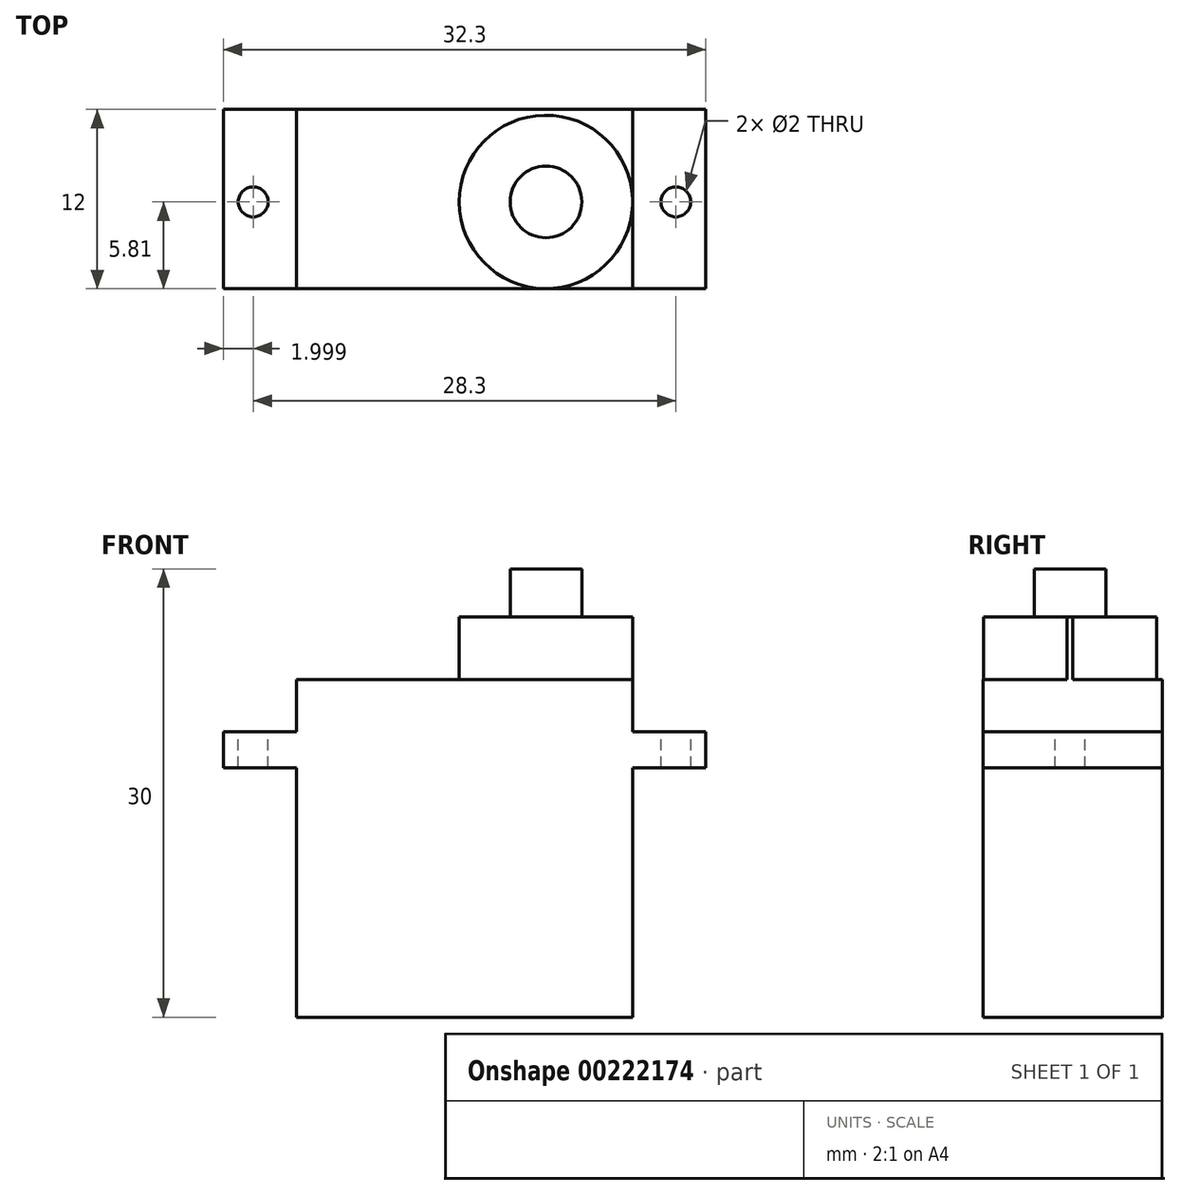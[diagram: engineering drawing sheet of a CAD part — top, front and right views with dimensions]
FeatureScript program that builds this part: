
annotation { "Feature Type Name" : "Feature", "Feature Type Description" : "" }
export const myFeature = defineFeature(function(context is Context, id is Id, definition is map)
    precondition{}
    {
        {
            var Q0;
            Q0=qCreatedBy(makeId("Top.planeOp"),FACE);
            var sketch = newSketch(context, id + "F0", { "sketchPlane" : qUnion([Q0])});
            skLineSegment(sketch, "E0.bottom", {"start": v(-11.12, 6.19) * mm, "end": v(21.18, 6.19) * mm});
            skLineSegment(sketch, "E0.top", {"start": v(-11.12, -5.81) * mm, "end": v(21.18, -5.81) * mm});
            skLineSegment(sketch, "E0.left", {"start": v(-11.12, 6.19) * mm, "end": v(-11.12, -5.81) * mm});
            skLineSegment(sketch, "E0.right", {"start": v(21.18, 6.19) * mm, "end": v(21.18, -5.81) * mm});
            skSolve(sketch);
        }
        {
            var Q0;
            Q0=makeQuery(id+"F0.imprint","IMPRINT",FACE,{"disambiguationData":[TD([[makeQuery(id+"F0.imprint","IMPRINT",EDGE,{"derivedFrom":sQuery(id+"F0.wireOp",EDGE,"E0.bottom")}),-1.0]])]});
            extrude(context, id + "F1", {"entities" : qUnion([Q0]), "depth" : 2.4 * mm});
        }
        {
            var Q0;
            Q0=makeQuery(id+"F1.opExtrude","CAP_FACE",FACE,{"disambiguationData":[OSD([sQuery(id+"F0.wireOp",EDGE,"E0.bottom"),sQuery(id+"F0.wireOp",EDGE,"E0.top"),sQuery(id+"F0.wireOp",EDGE,"E0.left"),sQuery(id+"F0.wireOp",EDGE,"E0.right")])],"isStart":false});
            var sketch = newSketch(context, id + "F2", { "sketchPlane" : qUnion([Q0])});
            skLineSegment(sketch, "E1.bottom", {"start": v(-6.22, 6.19) * mm, "end": v(16.28, 6.19) * mm});
            skLineSegment(sketch, "E1.top", {"start": v(-6.22, -5.81) * mm, "end": v(16.28, -5.81) * mm});
            skLineSegment(sketch, "E1.left", {"start": v(-6.22, 6.19) * mm, "end": v(-6.22, -5.81) * mm});
            skLineSegment(sketch, "E1.right", {"start": v(16.28, 6.19) * mm, "end": v(16.28, -5.81) * mm});
            skLineSegment(sketch, "E2", {"start": v(5.03, 6.19) * mm, "end": v(5.03, -10) * mm, "construction": true});
            skPoint(sketch, "E2.endSnap0", {"position": v(5.03, -5.81) * mm});
            skSolve(sketch);
        }
        {
            var Q0;
            Q0=makeQuery(id+"F2.imprint","IMPRINT",FACE,{"disambiguationData":[TD([[makeQuery(id+"F2.imprint","IMPRINT",EDGE,{"derivedFrom":sQuery(id+"F2.wireOp",EDGE,"E1.bottom")}),-1.0]])]});
            extrude(context, id + "F3", {"entities" : qUnion([Q0]), "operationType" : NewBodyOperationType.ADD, "depth" : 3.5 * mm});
        }
        {
            var Q0;
            Q0=makeQuery(id+"F3.opExtrude","CAP_FACE",FACE,{"disambiguationData":[OSD([sQuery(id+"F2.wireOp",EDGE,"E1.bottom"),sQuery(id+"F2.wireOp",EDGE,"E1.top"),sQuery(id+"F2.wireOp",EDGE,"E1.left"),sQuery(id+"F2.wireOp",EDGE,"E1.right")])],"isStart":false});
            extrude(context, id + "F4", {"entities" : qUnion([Q0]), "operationType" : NewBodyOperationType.ADD, "oppositeDirection" : true, "depth" : 22.6 * mm});
        }
        {
            var Q0;
            Q0=makeQuery(id+"F3.opExtrude","CAP_FACE",FACE,{"disambiguationData":[OSD([sQuery(id+"F2.wireOp",EDGE,"E1.bottom"),sQuery(id+"F2.wireOp",EDGE,"E1.top"),sQuery(id+"F2.wireOp",EDGE,"E1.left"),sQuery(id+"F2.wireOp",EDGE,"E1.right")])],"isStart":false});
            var sketch = newSketch(context, id + "F5", { "sketchPlane" : qUnion([Q0])});
            skCircle(sketch, "E3", {"center": v(10.48, 0) * mm, "radius": 5.8 * mm});
            skSolve(sketch);
        }
        {
            var Q0;
            {var subQ0=sQuery(id+"F5.wireOp",EDGE,"E3");var subQ1=makeQuery(id+"F3.opExtrude","CAP_EDGE",EDGE,{"disambiguationData":[OSD([sQuery(id+"F2.wireOp",EDGE,"E1.right")])],"isStart":false});var subQ2=makeQuery(id+"F5.imprint","INTERSECT",VERTEX,{"disambiguationData":[OD(0.0)],"derivedFrom":[subQ1,subQ0]});Q0=makeQuery(id+"F5.imprint","IMPRINT",FACE,{"disambiguationData":[TD([[makeQuery(id+"F5.imprint","IMPRINT",EDGE,{"disambiguationData":[TD([[subQ2,-1.0]])],"derivedFrom":subQ0}),1.0]])]});}
            extrude(context, id + "F6", {"entities" : qUnion([Q0]), "operationType" : NewBodyOperationType.ADD, "depth" : 4.2 * mm});
        }
        {
            var Q0;
            Q0=makeQuery(id+"F6.opExtrude","CAP_FACE",FACE,{"disambiguationData":[OSD([sQuery(id+"F2.wireOp",EDGE,"E1.right"),sQuery(id+"F5.wireOp",EDGE,"E3")])],"isStart":false});
            var sketch = newSketch(context, id + "F7", { "sketchPlane" : qUnion([Q0])});
            skCircle(sketch, "E4", {"center": v(10.48, 0) * mm, "radius": 2.4 * mm});
            skSolve(sketch);
        }
        {
            var Q0;
            Q0=makeQuery(id+"F7.imprint","IMPRINT",FACE,{"disambiguationData":[TD([[makeQuery(id+"F7.imprint","IMPRINT",EDGE,{"derivedFrom":sQuery(id+"F7.wireOp",EDGE,"E4")}),1.0]])]});
            extrude(context, id + "F8", {"entities" : qUnion([Q0]), "operationType" : NewBodyOperationType.ADD, "depth" : 3.2 * mm});
        }
        {
            var Q0;
            {var subQ0=sQuery(id+"F0.wireOp",EDGE,"E0.left");var subQ1=sQuery(id+"F0.wireOp",EDGE,"E0.top");var subQ2=sQuery(id+"F0.wireOp",EDGE,"E0.bottom");Q0=makeQuery(id+"F3.boolean.opBoolean","SPLIT",FACE,{"disambiguationData":[TD([makeQuery(id+"F1.opExtrude","SWEPT_FACE",FACE,{"disambiguationData":[OSD([subQ0])]})])],"derivedFrom":makeQuery(id+"F1.opExtrude","CAP_FACE",FACE,{"disambiguationData":[OSD([subQ2,subQ1,subQ0,sQuery(id+"F0.wireOp",EDGE,"E0.right")])],"isStart":false})});}
            var sketch = newSketch(context, id + "F9", { "sketchPlane" : qUnion([Q0])});
            skCircle(sketch, "E5", {"center": v(-9.12, 0) * mm, "radius": 1 * mm});
            skCircle(sketch, "E6", {"center": v(19.18, 0) * mm, "radius": 1 * mm});
            skSolve(sketch);
        }
        {
            var Q0;
            Q0=makeQuery(id+"F9.imprint","IMPRINT",FACE,{"disambiguationData":[TD([[makeQuery(id+"F9.imprint","IMPRINT",EDGE,{"derivedFrom":sQuery(id+"F9.wireOp",EDGE,"E5")}),1.0]])]});
            var Q1;
            Q1=makeQuery(id+"F9.imprint","IMPRINT",FACE,{"disambiguationData":[TD([[makeQuery(id+"F9.imprint","IMPRINT",EDGE,{"derivedFrom":sQuery(id+"F9.wireOp",EDGE,"E6")}),1.0]])]});
            extrude(context, id + "F10", {"entities" : qUnion([Q0, Q1]), "operationType" : NewBodyOperationType.REMOVE, "oppositeDirection" : true, "depth" : 3 * mm});
        }
    });
